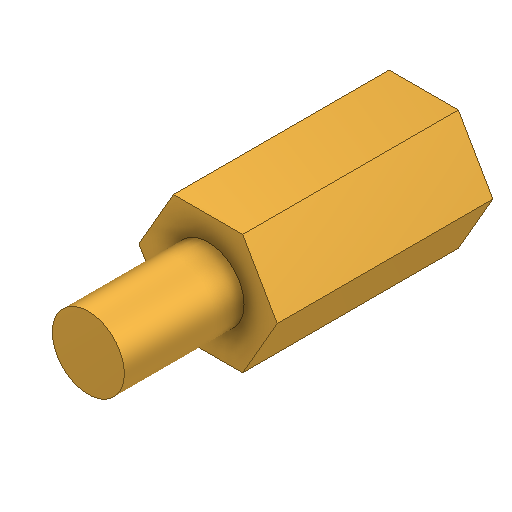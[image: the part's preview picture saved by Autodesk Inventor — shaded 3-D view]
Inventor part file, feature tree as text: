
AUTODESK INVENTOR PART (.ipt)
format: ipt  version: 2025.2 (Build 292293000, 293)  size: 118,784 bytes
history: native  units: mm
features: extrude x2, sketch x2
ambient origin geometry x8: Origin, YZ Plane, XZ Plane, XY Plane, X Axis, Y Axis, Z Axis, Center Point
bodies: Solid1 (feature_tree)
feature tree (4):
  extrude  "Extrusion1"  Depth=5.0mm
  extrude  "Extrusion2"  Depth=5.0mm TaperAngle=0.0deg
  sketch  "Sketch1"  dims[d0=5.0mm d1=3.0mm]
  sketch  "Sketch2"  dims[d2=9.0mm d3=0.0mm d4=5.0mm d5=0.0mm]
